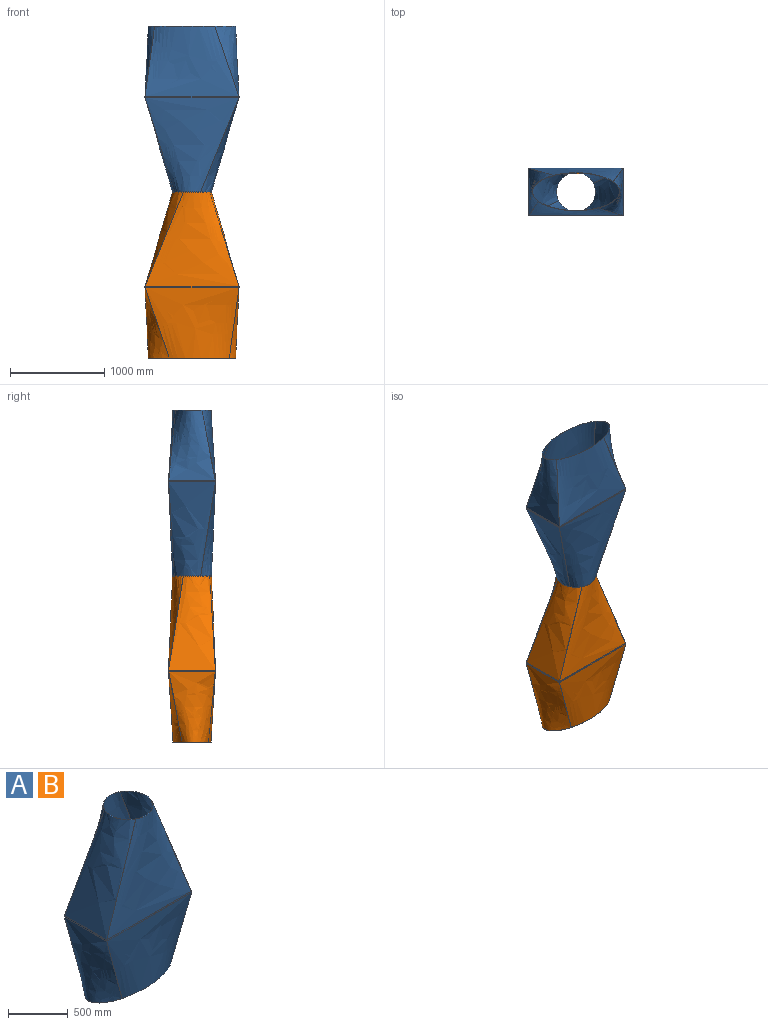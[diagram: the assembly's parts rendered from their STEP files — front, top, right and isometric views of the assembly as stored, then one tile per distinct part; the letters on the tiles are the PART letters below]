
ASSEMBLY  parts=2 mates=1
PART A: 26 faces, bbox 1025x515x1787.5 mm
  f0: plane 500x15mm, normal (-1,0,0), area 7500mm2, adj f1,f3,f5,f13
  f1: plane 1000x15mm, normal (0,-1,0), area 15000mm2, adj f0,f2,f6,f12
  f2: plane 500x15mm, normal (1,0,0), area 7500mm2, adj f1,f3,f7,f11
  f3: plane 1000x15mm, normal (0,1,0), area 15000mm2, adj f0,f2,f8,f10
  f4: plane 415.85x415.85mm, normal (0,0,1), area 3326mm2, adj f5,f6,f7,f8,f18,f19,f20,f21
  f5: bspline ~1000x505mm, area 422576.6mm2, adj f0,f4,f6,f8
  f6: bspline ~1020x1000mm, area 653501.2mm2, adj f1,f4,f5,f7
  f7: bspline ~1000x505mm, area 422576.6mm2, adj f2,f4,f6,f8
  f8: bspline ~1010x1000mm, area 653501.2mm2, adj f3,f4,f5,f7
  f9: plane 930.06x404.74mm, normal (0,0,-1), area 5459.7mm2, adj f10,f11,f12,f13,f22,f23,f24,f25
  f10: bspline ~1010x750mm, area 622300.4mm2, adj f3,f9,f11,f13
  f11: bspline ~750x505mm, area 332325.5mm2, adj f2,f9,f10,f12
  f12: bspline ~1010x750mm, area 622300.4mm2, adj f1,f9,f11,f13
  f13: bspline ~750x505mm, area 332325.5mm2, adj f0,f9,f10,f12
  f14: plane 495.12x14.7mm, normal (1,0,0), area 7155.3mm2, adj f15,f17,f18,f22,f25
  f15: plane 995.15x15.02mm, normal (0,1,0), area 14714.7mm2, adj f14,f16,f18,f19,f20,f24,f25
  f16: plane 495.12x14.7mm, normal (-1,0,0), area 7155.3mm2, adj f15,f17,f20,f23,f24
  f17: plane 995.15x15.02mm, normal (0,-1,0), area 14714.7mm2, adj f14,f16,f18,f20,f21,f22,f23
  f18: offset ~1015x515mm, area 417984.4mm2, adj f4,f14,f15,f17,f19,f21
  f19: offset ~1025x1015mm, area 649078.8mm2, adj f4,f15,f18,f20
  f20: offset ~1015x515mm, area 417984.4mm2, adj f4,f15,f16,f17,f19,f21
  f21: offset ~1025x1015mm, area 649078.7mm2, adj f4,f17,f18,f20
  f22: offset ~1025x762.5mm, area 619892.4mm2, adj f9,f14,f17,f23,f25
  f23: offset ~762.5x515mm, area 328426.8mm2, adj f9,f16,f17,f22,f24
  f24: offset ~1025x762.5mm, area 619892.5mm2, adj f9,f15,f16,f23,f25
  f25: offset ~762.5x515mm, area 328426.8mm2, adj f9,f14,f15,f22,f24
PART B: same geometry as A
PLACE A rot(axis=(1,0,0),180deg) t=(765.94,691.62,2027.82)mm
PLACE B t=(765.94,691.79,-2.18)mm
MATE fastened A.f4 <-> B.f4  axis (0,0,-1) through (765.85,691.7,1012.82)mm
